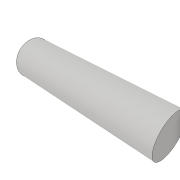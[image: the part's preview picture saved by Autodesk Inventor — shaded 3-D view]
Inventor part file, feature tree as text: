
AUTODESK INVENTOR PART (.ipt)
format: ipt  version: 2017 (Build 210142000, 142)  size: 72,192 bytes
history: native  units: in
note: dims shown in document units (in); Inventor stores cm internally (conversion verified against a paired STEP export)
features: sketch x2, extrude x1
ambient origin geometry x8: Origin, YZ Plane, XZ Plane, XY Plane, X Axis, Y Axis, Z Axis, Center Point
bodies: Solid1 (feature_tree)
feature tree (3):
  sketch  "Sketch1"  dims[d0=0.1575in d1=0.5906in d2=0.0in]
  extrude  "Extrusion1"  Depth=0.5906in TaperAngle=0.0deg
  sketch  "Sketch2"
